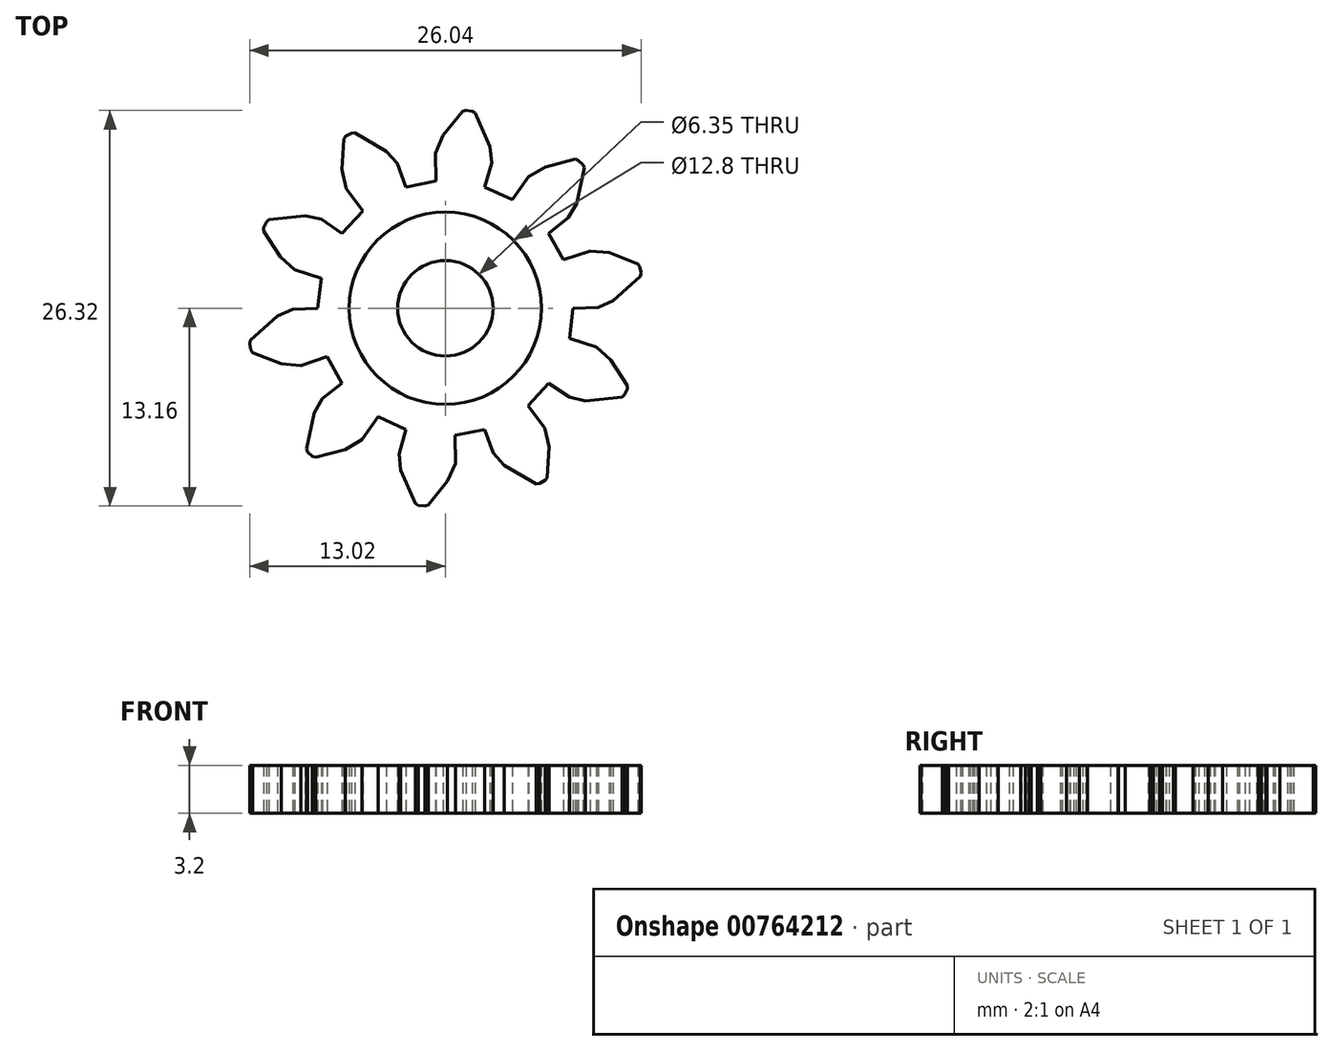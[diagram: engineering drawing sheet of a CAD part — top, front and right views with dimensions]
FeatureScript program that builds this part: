
annotation { "Feature Type Name" : "Feature", "Feature Type Description" : "" }
export const myFeature = defineFeature(function(context is Context, id is Id, definition is map)
    precondition{}
    {
        {
            var Q0;
            Q0=qCreatedBy(makeId("Top.planeOp"),FACE);
            var sketch = newSketch(context, id + "F0", { "sketchPlane" : qUnion([Q0])});
            skLineSegment(sketch, "E0", {"start": v(8.49, 0) * mm, "end": v(10.15, 0.06) * mm});
            skLineSegment(sketch, "E1", {"start": v(10.15, 0.06) * mm, "end": v(11.16, 0.5) * mm});
            skLineSegment(sketch, "E2", {"start": v(11.16, 0.5) * mm, "end": v(12.98, 2.13) * mm});
            skLineSegment(sketch, "E3", {"start": v(12.98, 2.13) * mm, "end": v(13.02, 2.35) * mm});
            skLineSegment(sketch, "E4", {"start": v(13.02, 2.35) * mm, "end": v(12.94, 2.77) * mm});
            skLineSegment(sketch, "E5", {"start": v(12.94, 2.77) * mm, "end": v(12.81, 2.95) * mm});
            skLineSegment(sketch, "E6", {"start": v(12.81, 2.95) * mm, "end": v(10.9, 3.7) * mm});
            skLineSegment(sketch, "E7", {"start": v(10.9, 3.7) * mm, "end": v(9.62, 3.82) * mm});
            skLineSegment(sketch, "E8", {"start": v(9.62, 3.82) * mm, "end": v(7.85, 3.22) * mm});
            skLineSegment(sketch, "E9", {"start": v(7.85, 3.22) * mm, "end": v(6.87, 4.99) * mm});
            skLineSegment(sketch, "E10", {"start": v(6.87, 4.99) * mm, "end": v(8.18, 6.02) * mm});
            skLineSegment(sketch, "E11", {"start": v(8.18, 6.02) * mm, "end": v(8.73, 6.97) * mm});
            skLineSegment(sketch, "E12", {"start": v(8.73, 6.97) * mm, "end": v(9.25, 9.35) * mm});
            skLineSegment(sketch, "E13", {"start": v(9.25, 9.35) * mm, "end": v(9.15, 9.55) * mm});
            skLineSegment(sketch, "E14", {"start": v(9.15, 9.55) * mm, "end": v(8.84, 9.84) * mm});
            skLineSegment(sketch, "E15", {"start": v(8.84, 9.84) * mm, "end": v(8.63, 9.92) * mm});
            skLineSegment(sketch, "E16", {"start": v(8.63, 9.92) * mm, "end": v(6.65, 9.4) * mm});
            skLineSegment(sketch, "E17", {"start": v(6.65, 9.4) * mm, "end": v(5.54, 8.74) * mm});
            skLineSegment(sketch, "E18", {"start": v(5.54, 8.74) * mm, "end": v(4.46, 7.22) * mm});
            skLineSegment(sketch, "E19", {"start": v(4.46, 7.22) * mm, "end": v(2.62, 8.07) * mm});
            skLineSegment(sketch, "E20", {"start": v(2.62, 8.07) * mm, "end": v(3.08, 9.67) * mm});
            skLineSegment(sketch, "E21", {"start": v(3.08, 9.67) * mm, "end": v(2.97, 10.77) * mm});
            skLineSegment(sketch, "E22", {"start": v(2.97, 10.77) * mm, "end": v(1.98, 13) * mm});
            skLineSegment(sketch, "E23", {"start": v(1.98, 13) * mm, "end": v(1.79, 13.1) * mm});
            skLineSegment(sketch, "E24", {"start": v(1.79, 13.1) * mm, "end": v(1.37, 13.16) * mm});
            skLineSegment(sketch, "E25", {"start": v(1.37, 13.16) * mm, "end": v(1.15, 13.1) * mm});
            skLineSegment(sketch, "E26", {"start": v(1.15, 13.1) * mm, "end": v(-0.15, 11.5) * mm});
            skLineSegment(sketch, "E27", {"start": v(-0.15, 11.5) * mm, "end": v(-0.66, 10.33) * mm});
            skLineSegment(sketch, "E28", {"start": v(-0.66, 10.33) * mm, "end": v(-0.64, 8.46) * mm});
            skLineSegment(sketch, "E29", {"start": v(-0.64, 8.46) * mm, "end": v(-2.62, 8.07) * mm});
            skLineSegment(sketch, "E30", {"start": v(-2.62, 8.07) * mm, "end": v(-3.2, 9.64) * mm});
            skLineSegment(sketch, "E31", {"start": v(-3.2, 9.64) * mm, "end": v(-3.93, 10.46) * mm});
            skLineSegment(sketch, "E32", {"start": v(-3.93, 10.46) * mm, "end": v(-6.04, 11.68) * mm});
            skLineSegment(sketch, "E33", {"start": v(-6.04, 11.68) * mm, "end": v(-6.26, 11.66) * mm});
            skLineSegment(sketch, "E34", {"start": v(-6.26, 11.66) * mm, "end": v(-6.63, 11.45) * mm});
            skLineSegment(sketch, "E35", {"start": v(-6.63, 11.45) * mm, "end": v(-6.77, 11.27) * mm});
            skLineSegment(sketch, "E36", {"start": v(-6.77, 11.27) * mm, "end": v(-6.88, 9.23) * mm});
            skLineSegment(sketch, "E37", {"start": v(-6.88, 9.23) * mm, "end": v(-6.6, 7.97) * mm});
            skLineSegment(sketch, "E38", {"start": v(-6.6, 7.97) * mm, "end": v(-5.5, 6.47) * mm});
            skLineSegment(sketch, "E39", {"start": v(-5.5, 6.47) * mm, "end": v(-6.87, 4.99) * mm});
            skLineSegment(sketch, "E40", {"start": v(-6.87, 4.99) * mm, "end": v(-8.25, 5.92) * mm});
            skLineSegment(sketch, "E41", {"start": v(-8.25, 5.92) * mm, "end": v(-9.32, 6.15) * mm});
            skLineSegment(sketch, "E42", {"start": v(-9.32, 6.15) * mm, "end": v(-11.75, 5.9) * mm});
            skLineSegment(sketch, "E43", {"start": v(-11.75, 5.9) * mm, "end": v(-11.91, 5.75) * mm});
            skLineSegment(sketch, "E44", {"start": v(-11.91, 5.75) * mm, "end": v(-12.1, 5.36) * mm});
            skLineSegment(sketch, "E45", {"start": v(-12.1, 5.36) * mm, "end": v(-12.1, 5.14) * mm});
            skLineSegment(sketch, "E46", {"start": v(-12.1, 5.14) * mm, "end": v(-11, 3.42) * mm});
            skLineSegment(sketch, "E47", {"start": v(-11, 3.42) * mm, "end": v(-10.03, 2.56) * mm});
            skLineSegment(sketch, "E48", {"start": v(-10.03, 2.56) * mm, "end": v(-8.25, 2) * mm});
            skLineSegment(sketch, "E49", {"start": v(-8.25, 2) * mm, "end": v(-8.49, 0) * mm});
            skLineSegment(sketch, "E50", {"start": v(-8.49, 0) * mm, "end": v(-10.15, -0.06) * mm});
            skLineSegment(sketch, "E51", {"start": v(-10.15, -0.06) * mm, "end": v(-11.16, -0.5) * mm});
            skLineSegment(sketch, "E52", {"start": v(-11.16, -0.5) * mm, "end": v(-12.98, -2.13) * mm});
            skLineSegment(sketch, "E53", {"start": v(-12.98, -2.13) * mm, "end": v(-13.02, -2.35) * mm});
            skLineSegment(sketch, "E54", {"start": v(-13.02, -2.35) * mm, "end": v(-12.94, -2.77) * mm});
            skLineSegment(sketch, "E55", {"start": v(-12.94, -2.77) * mm, "end": v(-12.81, -2.95) * mm});
            skLineSegment(sketch, "E56", {"start": v(-12.81, -2.95) * mm, "end": v(-10.9, -3.7) * mm});
            skLineSegment(sketch, "E57", {"start": v(-10.9, -3.7) * mm, "end": v(-9.62, -3.82) * mm});
            skLineSegment(sketch, "E58", {"start": v(-9.62, -3.82) * mm, "end": v(-7.85, -3.22) * mm});
            skLineSegment(sketch, "E59", {"start": v(-7.85, -3.22) * mm, "end": v(-6.87, -4.99) * mm});
            skLineSegment(sketch, "E60", {"start": v(-6.87, -4.99) * mm, "end": v(-8.18, -6.02) * mm});
            skLineSegment(sketch, "E61", {"start": v(-8.18, -6.02) * mm, "end": v(-8.73, -6.97) * mm});
            skLineSegment(sketch, "E62", {"start": v(-8.73, -6.97) * mm, "end": v(-9.25, -9.35) * mm});
            skLineSegment(sketch, "E63", {"start": v(-9.25, -9.35) * mm, "end": v(-9.15, -9.55) * mm});
            skLineSegment(sketch, "E64", {"start": v(-9.15, -9.55) * mm, "end": v(-8.84, -9.84) * mm});
            skLineSegment(sketch, "E65", {"start": v(-8.84, -9.84) * mm, "end": v(-8.63, -9.92) * mm});
            skLineSegment(sketch, "E66", {"start": v(-8.63, -9.92) * mm, "end": v(-6.65, -9.4) * mm});
            skLineSegment(sketch, "E67", {"start": v(-6.65, -9.4) * mm, "end": v(-5.54, -8.74) * mm});
            skLineSegment(sketch, "E68", {"start": v(-5.54, -8.74) * mm, "end": v(-4.46, -7.22) * mm});
            skLineSegment(sketch, "E69", {"start": v(-4.46, -7.22) * mm, "end": v(-2.62, -8.07) * mm});
            skLineSegment(sketch, "E70", {"start": v(-2.62, -8.07) * mm, "end": v(-3.08, -9.67) * mm});
            skLineSegment(sketch, "E71", {"start": v(-3.08, -9.67) * mm, "end": v(-2.97, -10.77) * mm});
            skLineSegment(sketch, "E72", {"start": v(-2.97, -10.77) * mm, "end": v(-1.98, -13) * mm});
            skLineSegment(sketch, "E73", {"start": v(-1.98, -13) * mm, "end": v(-1.79, -13.1) * mm});
            skLineSegment(sketch, "E74", {"start": v(-1.79, -13.1) * mm, "end": v(-1.37, -13.16) * mm});
            skLineSegment(sketch, "E75", {"start": v(-1.37, -13.16) * mm, "end": v(-1.15, -13.1) * mm});
            skLineSegment(sketch, "E76", {"start": v(-1.15, -13.1) * mm, "end": v(0.15, -11.5) * mm});
            skLineSegment(sketch, "E77", {"start": v(0.15, -11.5) * mm, "end": v(0.66, -10.33) * mm});
            skLineSegment(sketch, "E78", {"start": v(0.66, -10.33) * mm, "end": v(0.64, -8.46) * mm});
            skLineSegment(sketch, "E79", {"start": v(0.64, -8.46) * mm, "end": v(2.62, -8.07) * mm});
            skLineSegment(sketch, "E80", {"start": v(2.62, -8.07) * mm, "end": v(3.2, -9.64) * mm});
            skLineSegment(sketch, "E81", {"start": v(3.2, -9.64) * mm, "end": v(3.93, -10.46) * mm});
            skLineSegment(sketch, "E82", {"start": v(3.93, -10.46) * mm, "end": v(6.04, -11.68) * mm});
            skLineSegment(sketch, "E83", {"start": v(6.04, -11.68) * mm, "end": v(6.26, -11.66) * mm});
            skLineSegment(sketch, "E84", {"start": v(6.26, -11.66) * mm, "end": v(6.63, -11.45) * mm});
            skLineSegment(sketch, "E85", {"start": v(6.63, -11.45) * mm, "end": v(6.77, -11.27) * mm});
            skLineSegment(sketch, "E86", {"start": v(6.77, -11.27) * mm, "end": v(6.88, -9.23) * mm});
            skLineSegment(sketch, "E87", {"start": v(6.88, -9.23) * mm, "end": v(6.6, -7.97) * mm});
            skLineSegment(sketch, "E88", {"start": v(6.6, -7.97) * mm, "end": v(5.5, -6.47) * mm});
            skLineSegment(sketch, "E89", {"start": v(5.5, -6.47) * mm, "end": v(6.87, -4.99) * mm});
            skLineSegment(sketch, "E90", {"start": v(6.87, -4.99) * mm, "end": v(8.25, -5.92) * mm});
            skLineSegment(sketch, "E91", {"start": v(8.25, -5.92) * mm, "end": v(9.32, -6.15) * mm});
            skLineSegment(sketch, "E92", {"start": v(9.32, -6.15) * mm, "end": v(11.75, -5.9) * mm});
            skLineSegment(sketch, "E93", {"start": v(11.75, -5.9) * mm, "end": v(11.91, -5.75) * mm});
            skLineSegment(sketch, "E94", {"start": v(11.91, -5.75) * mm, "end": v(12.1, -5.36) * mm});
            skLineSegment(sketch, "E95", {"start": v(12.1, -5.36) * mm, "end": v(12.1, -5.14) * mm});
            skLineSegment(sketch, "E96", {"start": v(12.1, -5.14) * mm, "end": v(11, -3.42) * mm});
            skLineSegment(sketch, "E97", {"start": v(11, -3.42) * mm, "end": v(10.03, -2.56) * mm});
            skLineSegment(sketch, "E98", {"start": v(10.03, -2.56) * mm, "end": v(8.25, -2) * mm});
            skLineSegment(sketch, "E99", {"start": v(8.25, -2) * mm, "end": v(8.49, 0) * mm});
            skCircle(sketch, "E100", {"center": v(0, 0) * mm, "radius": 6.4 * mm});
            skCircle(sketch, "E101", {"center": v(0, 0) * mm, "radius": 11 * mm, "construction": true});
            skSolve(sketch);
        }
        {
            var Q0;
            Q0 = qSketchRegion(id + "F0", true);
            extrude(context, id + "F1", {"entities" : qUnion([Q0]), "endBound" : BoundingType.SYMMETRIC, "depth" : 3.2 * mm, "offsetDistance" : 25 * mm});
        }
        {
            var Q0;
            Q0=qCreatedBy(makeId("Top.planeOp"),FACE);
            var sketch = newSketch(context, id + "F2", { "sketchPlane" : qUnion([Q0])});
            skCircle(sketch, "E102", {"center": v(0, 0) * mm, "radius": 3.17 * mm});
            skCircle(sketch, "E103.0", {"center": v(0, 0) * mm, "radius": 6.4 * mm});
            skSolve(sketch);
        }
        {
            var Q0;
            Q0 = qSketchRegion(id + "F2", true);
            extrude(context, id + "F3", {"entities" : qUnion([Q0]), "endBound" : BoundingType.SYMMETRIC, "depth" : 3.2 * mm, "offsetDistance" : 25 * mm});
        }
    });
